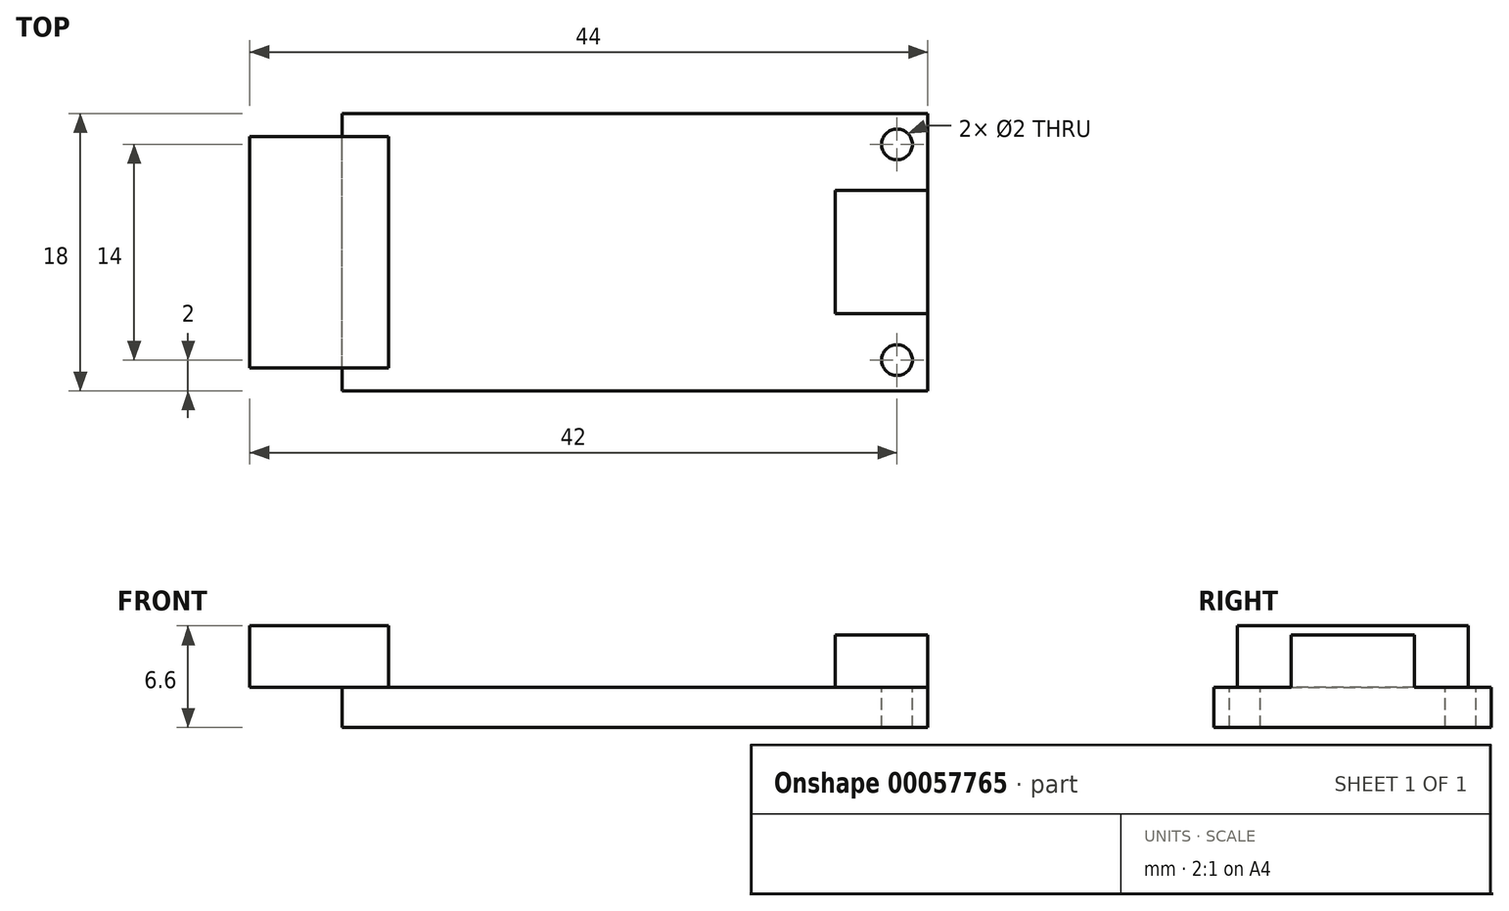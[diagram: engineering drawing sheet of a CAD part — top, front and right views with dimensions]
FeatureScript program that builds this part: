
annotation { "Feature Type Name" : "Feature", "Feature Type Description" : "" }
export const myFeature = defineFeature(function(context is Context, id is Id, definition is map)
    precondition{}
    {
        {
            var Q0;
            Q0=qCreatedBy(makeId("Top.planeOp"),FACE);
            var sketch = newSketch(context, id + "F0", { "sketchPlane" : qUnion([Q0])});
            skLineSegment(sketch, "E0.rect.bottom", {"start": v(19, -9) * mm, "end": v(-19, -9) * mm});
            skLineSegment(sketch, "E0.rect.top", {"start": v(19, 9) * mm, "end": v(-19, 9) * mm});
            skLineSegment(sketch, "E0.rect.left", {"start": v(19, -9) * mm, "end": v(19, 9) * mm});
            skLineSegment(sketch, "E0.rect.right", {"start": v(-19, -9) * mm, "end": v(-19, 9) * mm});
            skPoint(sketch, "E0.rect.middle", {"position": v(0, 0) * mm});
            skSolve(sketch);
        }
        {
            var Q0;
            Q0 = qSketchRegion(id + "F0", true);
            extrude(context, id + "F1", {"entities" : qUnion([Q0]), "depth" : 2.6 * mm});
        }
        {
            var Q0;
            Q0=makeQuery(id+"F1.opExtrude","CAP_FACE",FACE,{"disambiguationData":[OSD([sQuery(id+"F0.wireOp",EDGE,"E0.rect.bottom"),sQuery(id+"F0.wireOp",EDGE,"E0.rect.top"),sQuery(id+"F0.wireOp",EDGE,"E0.rect.left"),sQuery(id+"F0.wireOp",EDGE,"E0.rect.right")])],"isStart":false});
            var sketch = newSketch(context, id + "F2", { "sketchPlane" : qUnion([Q0])});
            skCircle(sketch, "E1", {"center": v(17, 7) * mm, "radius": 1 * mm});
            skLineSegment(sketch, "E2", {"start": v(0, 0) * mm, "end": v(23.36, 0) * mm, "construction": true});
            skCircle(sketch, "E3.MirrorC", {"center": v(17, -7) * mm, "radius": 1 * mm});
            skSolve(sketch);
        }
        {
            var Q0;
            Q0 = qSketchRegion(id + "F2", true);
            var Q1;
            Q1=makeQuery(id+"F1.opExtrude","SWEPT_BODY",BODY,{"disambiguationData":[OSD([sQuery(id+"F0.wireOp",EDGE,"E0.rect.bottom"),sQuery(id+"F0.wireOp",EDGE,"E0.rect.top"),sQuery(id+"F0.wireOp",EDGE,"E0.rect.left"),sQuery(id+"F0.wireOp",EDGE,"E0.rect.right")])]});
            extrude(context, id + "F3", {"entities" : qUnion([Q0]), "operationType" : NewBodyOperationType.REMOVE, "endBound" : BoundingType.UP_TO_BODY, "oppositeDirection" : true, "endBoundEntityBody" : qUnion([Q1]), "depth" : 25 * mm});
        }
        {
            var Q0;
            Q0=makeQuery(id+"F1.opExtrude","CAP_FACE",FACE,{"disambiguationData":[OSD([sQuery(id+"F0.wireOp",EDGE,"E0.rect.bottom"),sQuery(id+"F0.wireOp",EDGE,"E0.rect.top"),sQuery(id+"F0.wireOp",EDGE,"E0.rect.left"),sQuery(id+"F0.wireOp",EDGE,"E0.rect.right")])],"isStart":false});
            var sketch = newSketch(context, id + "F4", { "sketchPlane" : qUnion([Q0])});
            skLineSegment(sketch, "E4.bottom", {"start": v(13, 4) * mm, "end": v(19, 4) * mm});
            skLineSegment(sketch, "E4.top", {"start": v(13, -4) * mm, "end": v(19, -4) * mm});
            skLineSegment(sketch, "E4.left", {"start": v(13, 4) * mm, "end": v(13, -4) * mm});
            skLineSegment(sketch, "E4.right", {"start": v(19, 4) * mm, "end": v(19, -4) * mm});
            skSolve(sketch);
        }
        {
            var Q0;
            Q0=makeQuery(id+"F4.imprint","IMPRINT",FACE,{"disambiguationData":[TD([[makeQuery(id+"F4.imprint","IMPRINT",EDGE,{"derivedFrom":sQuery(id+"F4.wireOp",EDGE,"E4.bottom")}),-1.0]])]});
            extrude(context, id + "F5", {"entities" : qUnion([Q0]), "operationType" : NewBodyOperationType.ADD, "depth" : 3.4 * mm});
        }
        {
            var Q0;
            Q0=makeQuery(id+"F1.opExtrude","CAP_FACE",FACE,{"disambiguationData":[OSD([sQuery(id+"F0.wireOp",EDGE,"E0.rect.bottom"),sQuery(id+"F0.wireOp",EDGE,"E0.rect.top"),sQuery(id+"F0.wireOp",EDGE,"E0.rect.left"),sQuery(id+"F0.wireOp",EDGE,"E0.rect.right")])],"isStart":false});
            var sketch = newSketch(context, id + "F6", { "sketchPlane" : qUnion([Q0])});
            skLineSegment(sketch, "E5.bottom", {"start": v(-25, 7.5) * mm, "end": v(-16, 7.5) * mm});
            skLineSegment(sketch, "E5.top", {"start": v(-25, -7.5) * mm, "end": v(-16, -7.5) * mm});
            skLineSegment(sketch, "E5.left", {"start": v(-25, 7.5) * mm, "end": v(-25, -7.5) * mm});
            skLineSegment(sketch, "E5.right", {"start": v(-16, 7.5) * mm, "end": v(-16, -7.5) * mm});
            skSolve(sketch);
        }
        {
            var Q0;
            Q0 = qSketchRegion(id + "F6", true);
            extrude(context, id + "F7", {"entities" : qUnion([Q0]), "operationType" : NewBodyOperationType.ADD, "depth" : 4 * mm});
        }
    });
